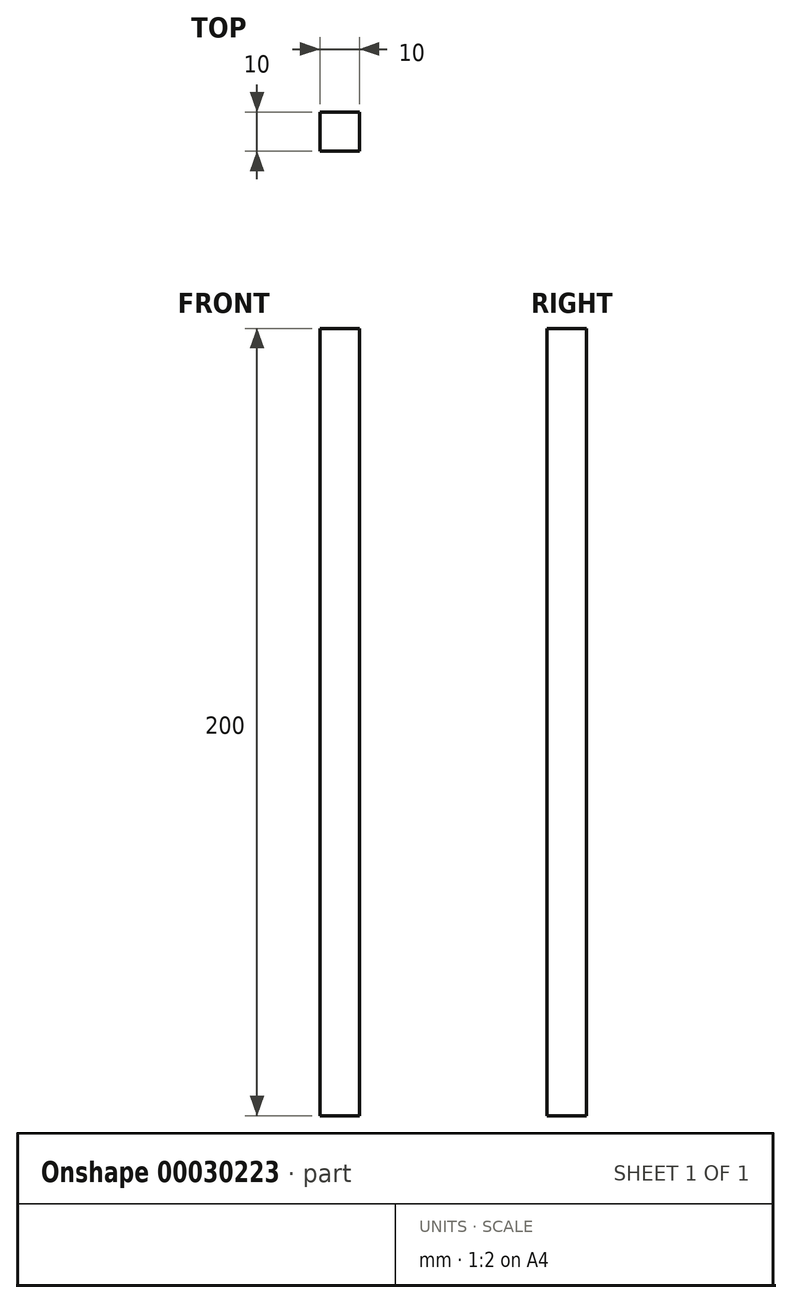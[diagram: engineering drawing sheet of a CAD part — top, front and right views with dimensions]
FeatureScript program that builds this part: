
annotation { "Feature Type Name" : "Feature", "Feature Type Description" : "" }
export const myFeature = defineFeature(function(context is Context, id is Id, definition is map)
    precondition{}
    {
        {
            var Q0;
            Q0=qCreatedBy(makeId("Top.planeOp"),FACE);
            var sketch = newSketch(context, id + "F0", { "sketchPlane" : qUnion([Q0])});
            skLineSegment(sketch, "E0.rect.bottom", {"start": v(-5, 5) * mm, "end": v(5, 5) * mm});
            skLineSegment(sketch, "E0.rect.top", {"start": v(-5, -5) * mm, "end": v(5, -5) * mm});
            skLineSegment(sketch, "E0.rect.left", {"start": v(-5, 5) * mm, "end": v(-5, -5) * mm});
            skLineSegment(sketch, "E0.rect.right", {"start": v(5, 5) * mm, "end": v(5, -5) * mm});
            skPoint(sketch, "E0.rect.middle", {"position": v(0, 0) * mm});
            skSolve(sketch);
        }
        {
            var Q0;
            Q0 = qSketchRegion(id + "F0", true);
            extrude(context, id + "F1", {"entities" : qUnion([Q0]), "depth" : 200 * mm});
        }
    });
